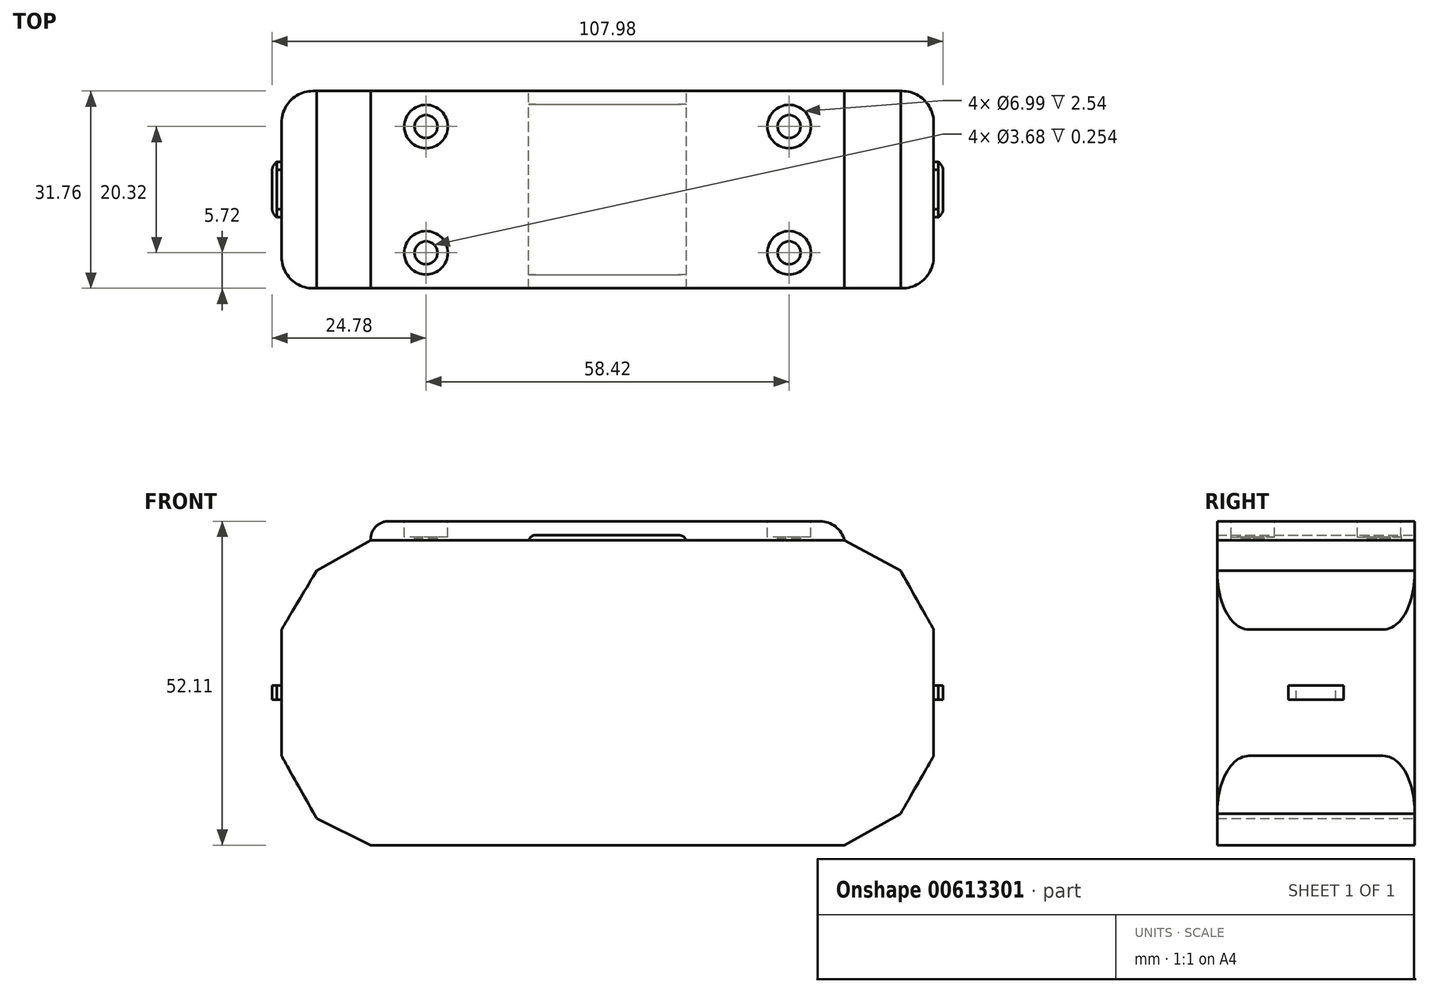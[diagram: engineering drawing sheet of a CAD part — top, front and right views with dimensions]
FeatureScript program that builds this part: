
annotation { "Feature Type Name" : "Feature", "Feature Type Description" : "" }
export const myFeature = defineFeature(function(context is Context, id is Id, definition is map)
    precondition{}
    {
        {
            var Q0;
            Q0=qCreatedBy(makeId("Front.planeOp"),FACE);
            var sketch = newSketch(context, id + "F0", { "sketchPlane" : qUnion([Q0])});
            skLineSegment(sketch, "E0", {"start": v(-38.1, 0) * mm, "end": v(0, 0) * mm});
            skLineSegment(sketch, "E1", {"start": v(0, 0) * mm, "end": v(38.1, 0) * mm});
            skLineSegment(sketch, "E2", {"start": v(-38.1, 0) * mm, "end": v(-52.47, 14.37) * mm});
            skLineSegment(sketch, "E3", {"start": v(38.1, 0) * mm, "end": v(52.47, 14.37) * mm});
            skLineSegment(sketch, "E4", {"start": v(-52.47, 14.37) * mm, "end": v(-52.47, 34.69) * mm});
            skLineSegment(sketch, "E5", {"start": v(52.47, 14.37) * mm, "end": v(52.47, 34.69) * mm});
            skLineSegment(sketch, "E6", {"start": v(-52.47, 34.69) * mm, "end": v(-38.1, 49.06) * mm});
            skLineSegment(sketch, "E7", {"start": v(52.47, 34.69) * mm, "end": v(38.1, 49.06) * mm});
            skLineSegment(sketch, "E8", {"start": v(38.1, 49.06) * mm, "end": v(12.7, 49.06) * mm});
            skLineSegment(sketch, "E9", {"start": v(-38.1, 49.06) * mm, "end": v(-12.7, 49.06) * mm});
            skLineSegment(sketch, "E10", {"start": v(-11.57, 49.9) * mm, "end": v(11.36, 49.9) * mm});
            skArc(sketch, "E11", {"start": v(-11.57, 49.9) * mm, "mid": v(-12.28, 49.66) * mm, "end": v(-12.7, 49.06) * mm});
            skArc(sketch, "E12", {"start": v(12.7, 49.06) * mm, "mid": v(12.15, 49.67) * mm, "end": v(11.36, 49.9) * mm});
            skLineSegment(sketch, "E13", {"start": v(-35.27, 52.11) * mm, "end": v(34.2, 52.11) * mm});
            skArc(sketch, "E14", {"start": v(-35.27, 52.11) * mm, "mid": v(-37.35, 51.2) * mm, "end": v(-38.1, 49.06) * mm});
            skArc(sketch, "E15", {"start": v(38.1, 49.06) * mm, "mid": v(36.67, 51.26) * mm, "end": v(34.2, 52.11) * mm});
            skLineSegment(sketch, "E16", {"start": v(-12.7, 49.06) * mm, "end": v(12.7, 49.06) * mm});
            skLineSegment(sketch, "E17", {"start": v(-52.47, 34.69) * mm, "end": v(-46.81, 44.17) * mm});
            skLineSegment(sketch, "E18", {"start": v(-46.81, 44.17) * mm, "end": v(-38.1, 49.06) * mm});
            skLineSegment(sketch, "E19", {"start": v(52.47, 34.69) * mm, "end": v(47.15, 44.17) * mm});
            skLineSegment(sketch, "E20", {"start": v(47.15, 44.17) * mm, "end": v(38.1, 49.06) * mm});
            skLineSegment(sketch, "E21", {"start": v(-52.47, 14.37) * mm, "end": v(-46.81, 4.29) * mm});
            skLineSegment(sketch, "E22", {"start": v(-46.81, 4.29) * mm, "end": v(-38.1, 0) * mm});
            skLineSegment(sketch, "E23", {"start": v(38.1, 0) * mm, "end": v(47.15, 5.08) * mm});
            skLineSegment(sketch, "E24", {"start": v(47.15, 5.08) * mm, "end": v(52.47, 14.37) * mm});
            skSolve(sketch);
        }
        {
            var Q0;
            Q0=makeQuery(id+"F0.imprint","IMPRINT",FACE,{"disambiguationData":[TD([[makeQuery(id+"F0.imprint","IMPRINT",EDGE,{"derivedFrom":sQuery(id+"F0.wireOp",EDGE,"E0")}),1.0]])]});
            var Q1;
            Q1=makeQuery(id+"F0.imprint","IMPRINT",FACE,{"disambiguationData":[TD([[makeQuery(id+"F0.imprint","IMPRINT",EDGE,{"derivedFrom":sQuery(id+"F0.wireOp",EDGE,"E2")}),1.0]])]});
            var Q2;
            Q2=makeQuery(id+"F0.imprint","IMPRINT",FACE,{"disambiguationData":[TD([[makeQuery(id+"F0.imprint","IMPRINT",EDGE,{"derivedFrom":sQuery(id+"F0.wireOp",EDGE,"E6")}),1.0]])]});
            var Q3;
            Q3=makeQuery(id+"F0.imprint","IMPRINT",FACE,{"disambiguationData":[TD([[makeQuery(id+"F0.imprint","IMPRINT",EDGE,{"derivedFrom":sQuery(id+"F0.wireOp",EDGE,"E7")}),-1.0]])]});
            var Q4;
            Q4=makeQuery(id+"F0.imprint","IMPRINT",FACE,{"disambiguationData":[TD([[makeQuery(id+"F0.imprint","IMPRINT",EDGE,{"derivedFrom":sQuery(id+"F0.wireOp",EDGE,"E3")}),-1.0]])]});
            extrude(context, id + "F1", {"entities" : qUnion([Q0, Q1, Q2, Q3, Q4]), "endBound" : BoundingType.SYMMETRIC, "depth" : 31.75 * mm, "offsetDistance" : 25.4 * mm});
        }
        {
            var Q0;
            Q0=makeQuery(id+"F0.imprint","IMPRINT",FACE,{"disambiguationData":[TD([[makeQuery(id+"F0.imprint","IMPRINT",EDGE,{"derivedFrom":sQuery(id+"F0.wireOp",EDGE,"E8")}),-1.0]])]});
            extrude(context, id + "F2", {"entities" : qUnion([Q0]), "endBound" : BoundingType.SYMMETRIC, "depth" : 31.75 * mm, "offsetDistance" : 25.4 * mm});
        }
        {
            var Q0;
            Q0=makeQuery(id+"F0.imprint","IMPRINT",FACE,{"disambiguationData":[TD([[makeQuery(id+"F0.imprint","IMPRINT",EDGE,{"derivedFrom":sQuery(id+"F0.wireOp",EDGE,"E10")}),-1.0]])]});
            extrude(context, id + "F3", {"entities" : qUnion([Q0]), "endBound" : BoundingType.SYMMETRIC, "depth" : 27.43 * mm, "offsetDistance" : 25.4 * mm});
        }
        {
            var Q0;
            Q0=makeQuery(id+"F2.opExtrude","SWEPT_FACE",FACE,{"disambiguationData":[OSD([sQuery(id+"F0.wireOp",EDGE,"E13")])]});
            var sketch = newSketch(context, id + "F4", { "sketchPlane" : qUnion([Q0])});
            skCircle(sketch, "E25", {"center": v(-29.2, 10.16) * mm, "radius": 3.5 * mm});
            skCircle(sketch, "E26", {"center": v(29.21, 10.16) * mm, "radius": 3.5 * mm});
            skCircle(sketch, "E27", {"center": v(-29.21, -10.16) * mm, "radius": 3.5 * mm});
            skCircle(sketch, "E28", {"center": v(29.21, -10.16) * mm, "radius": 3.5 * mm});
            skCircle(sketch, "E29", {"center": v(29.21, 10.16) * mm, "radius": 1.84 * mm});
            skCircle(sketch, "E30", {"center": v(-29.2, 10.16) * mm, "radius": 1.84 * mm});
            skCircle(sketch, "E31", {"center": v(-29.21, -10.16) * mm, "radius": 1.84 * mm});
            skCircle(sketch, "E32", {"center": v(29.21, -10.16) * mm, "radius": 1.84 * mm});
            skSolve(sketch);
        }
        {
            var Q0;
            {var subQ0=sQuery(id+"F4.wireOp",EDGE,"i9I5KANn-Hw2T-OKhb-yl4n-6DxJZw7aqsBT");var subQ1=sQuery(id+"F4.wireOp",EDGE,"TPdn8FKf-1Wfh-jzqV-Iljf-ABfrrcG5fK8c");var subQ2=makeQuery(id+"F4.imprint","INTERSECT",VERTEX,{"derivedFrom":[subQ1,subQ0]});Q0=makeQuery(id+"F4.imprint","IMPRINT",FACE,{"disambiguationData":[TD([[makeQuery(id+"F4.imprint","IMPRINT",EDGE,{"disambiguationData":[TD([[subQ2,1.0]])],"derivedFrom":subQ1}),-1.0]])]});}
            var Q1;
            {var subQ0=sQuery(id+"F4.wireOp",EDGE,"i9I5KANn-Hw2T-OKhb-yl4n-6DxJZw7aqsBT");var subQ1=sQuery(id+"F4.wireOp",EDGE,"TPdn8FKf-1Wfh-jzqV-Iljf-ABfrrcG5fK8c");var subQ2=makeQuery(id+"F4.imprint","INTERSECT",VERTEX,{"derivedFrom":[subQ1,subQ0]});Q1=makeQuery(id+"F4.imprint","IMPRINT",FACE,{"disambiguationData":[TD([[makeQuery(id+"F4.imprint","IMPRINT",EDGE,{"disambiguationData":[TD([[subQ2,1.0]])],"derivedFrom":subQ1}),1.0]])]});}
            var Q2;
            {var subQ0=sQuery(id+"F4.wireOp",EDGE,"VOcv5QYX-RCKe-hodg-bxS0-XieY8gz3RQ9G");var subQ1=sQuery(id+"F4.wireOp",EDGE,"O975SV0D-9PoP-xruf-v8xU-hlFepfZSX1na");var subQ2=makeQuery(id+"F4.imprint","INTERSECT",VERTEX,{"derivedFrom":[subQ1,subQ0]});Q2=makeQuery(id+"F4.imprint","IMPRINT",FACE,{"disambiguationData":[TD([[makeQuery(id+"F4.imprint","IMPRINT",EDGE,{"disambiguationData":[TD([[subQ2,1.0]])],"derivedFrom":subQ1}),-1.0]])]});}
            var Q3;
            {var subQ0=sQuery(id+"F4.wireOp",EDGE,"VOcv5QYX-RCKe-hodg-bxS0-XieY8gz3RQ9G");var subQ1=sQuery(id+"F4.wireOp",EDGE,"O975SV0D-9PoP-xruf-v8xU-hlFepfZSX1na");var subQ2=makeQuery(id+"F4.imprint","INTERSECT",VERTEX,{"derivedFrom":[subQ1,subQ0]});Q3=makeQuery(id+"F4.imprint","IMPRINT",FACE,{"disambiguationData":[TD([[makeQuery(id+"F4.imprint","IMPRINT",EDGE,{"disambiguationData":[TD([[subQ2,1.0]])],"derivedFrom":subQ1}),1.0]])]});}
            var Q4;
            Q4=makeQuery(id+"F4.imprint","IMPRINT",FACE,{"disambiguationData":[TD([[makeQuery(id+"F4.imprint","IMPRINT",EDGE,{"derivedFrom":sQuery(id+"F4.wireOp",EDGE,"E28")}),1.0]])]});
            var Q5;
            Q5=makeQuery(id+"F4.imprint","IMPRINT",FACE,{"disambiguationData":[TD([[makeQuery(id+"F4.imprint","IMPRINT",EDGE,{"derivedFrom":sQuery(id+"F4.wireOp",EDGE,"E27")}),1.0]])]});
            var Q6;
            Q6=makeQuery(id+"F4.imprint","IMPRINT",FACE,{"disambiguationData":[TD([[makeQuery(id+"F4.imprint","IMPRINT",EDGE,{"derivedFrom":sQuery(id+"F4.wireOp",EDGE,"E25")}),1.0]])]});
            var Q7;
            Q7=makeQuery(id+"F4.imprint","IMPRINT",FACE,{"disambiguationData":[TD([[makeQuery(id+"F4.imprint","IMPRINT",EDGE,{"derivedFrom":sQuery(id+"F4.wireOp",EDGE,"E26")}),1.0]])]});
            extrude(context, id + "F5", {"entities" : qUnion([Q0, Q1, Q2, Q3, Q4, Q5, Q6, Q7]), "operationType" : NewBodyOperationType.REMOVE, "oppositeDirection" : true, "depth" : 2.54 * mm, "offsetDistance" : 25.4 * mm});
        }
        {
            var Q0;
            Q0=makeQuery(id+"F4.imprint","IMPRINT",FACE,{"disambiguationData":[TD([[makeQuery(id+"F4.imprint","IMPRINT",EDGE,{"derivedFrom":sQuery(id+"F4.wireOp",EDGE,"E31")}),1.0]])]});
            var Q1;
            Q1=makeQuery(id+"F4.imprint","IMPRINT",FACE,{"disambiguationData":[TD([[makeQuery(id+"F4.imprint","IMPRINT",EDGE,{"derivedFrom":sQuery(id+"F4.wireOp",EDGE,"E29")}),1.0]])]});
            var Q2;
            Q2=makeQuery(id+"F4.imprint","IMPRINT",FACE,{"disambiguationData":[TD([[makeQuery(id+"F4.imprint","IMPRINT",EDGE,{"derivedFrom":sQuery(id+"F4.wireOp",EDGE,"E32")}),1.0]])]});
            var Q3;
            Q3=makeQuery(id+"F4.imprint","IMPRINT",FACE,{"disambiguationData":[TD([[makeQuery(id+"F4.imprint","IMPRINT",EDGE,{"derivedFrom":sQuery(id+"F4.wireOp",EDGE,"E30")}),1.0]])]});
            extrude(context, id + "F6", {"entities" : qUnion([Q0, Q1, Q2, Q3]), "operationType" : NewBodyOperationType.REMOVE, "oppositeDirection" : true, "depth" : 2.8 * mm, "offsetDistance" : 25.4 * mm});
        }
        {
            var Q0;
            Q0=makeQuery(id+"F1.opExtrude","SWEPT_FACE",FACE,{"disambiguationData":[OSD([sQuery(id+"F0.wireOp",EDGE,"E4")])]});
            var sketch = newSketch(context, id + "F7", { "sketchPlane" : qUnion([Q0])});
            skLineSegment(sketch, "E33", {"start": v(0, 34.69) * mm, "end": v(0, 14.37) * mm});
            skLineSegment(sketch, "E34", {"start": v(-15.88, 24.53) * mm, "end": v(15.88, 24.53) * mm});
            skLineSegment(sketch, "E35", {"start": v(-4.45, 24.53) * mm, "end": v(-4.45, 25.67) * mm});
            skLineSegment(sketch, "E36", {"start": v(4.45, 24.53) * mm, "end": v(4.45, 25.67) * mm});
            skLineSegment(sketch, "E37", {"start": v(4.45, 25.67) * mm, "end": v(3.18, 25.67) * mm});
            skLineSegment(sketch, "E38", {"start": v(3.18, 25.67) * mm, "end": v(3.18, 24.53) * mm});
            skLineSegment(sketch, "E39", {"start": v(-4.45, 25.67) * mm, "end": v(-3.18, 25.67) * mm});
            skLineSegment(sketch, "E40", {"start": v(-3.17, 25.67) * mm, "end": v(-3.17, 24.53) * mm});
            skLineSegment(sketch, "E41", {"start": v(-4.45, 24.53) * mm, "end": v(-4.45, 23.39) * mm});
            skLineSegment(sketch, "E42", {"start": v(4.45, 24.53) * mm, "end": v(4.45, 23.39) * mm});
            skLineSegment(sketch, "E43", {"start": v(-3.17, 24.53) * mm, "end": v(-3.17, 23.39) * mm});
            skLineSegment(sketch, "E44", {"start": v(-3.17, 23.39) * mm, "end": v(-4.45, 23.39) * mm});
            skLineSegment(sketch, "E45", {"start": v(3.18, 24.53) * mm, "end": v(3.18, 23.39) * mm});
            skLineSegment(sketch, "E46", {"start": v(3.18, 23.39) * mm, "end": v(4.45, 23.39) * mm});
            skLineSegment(sketch, "E47", {"start": v(3.18, 24.53) * mm, "end": v(-3.17, 24.53) * mm});
            skSolve(sketch);
        }
        {
            var Q0;
            {var subQ0=sQuery(id+"F7.wireOp",EDGE,"E35");Q0=makeQuery(id+"F7.imprint","IMPRINT",FACE,{"disambiguationData":[TD([[makeQuery(id+"F7.imprint","IMPRINT",EDGE,{"derivedFrom":subQ0}),-1.0]])]});}
            var Q1;
            {var subQ0=sQuery(id+"F7.wireOp",EDGE,"E41");Q1=makeQuery(id+"F7.imprint","IMPRINT",FACE,{"disambiguationData":[TD([[makeQuery(id+"F7.imprint","IMPRINT",EDGE,{"derivedFrom":subQ0}),1.0]])]});}
            var Q2;
            {var subQ0=sQuery(id+"F7.wireOp",EDGE,"E36");Q2=makeQuery(id+"F7.imprint","IMPRINT",FACE,{"disambiguationData":[TD([[makeQuery(id+"F7.imprint","IMPRINT",EDGE,{"derivedFrom":subQ0}),1.0]])]});}
            var Q3;
            {var subQ0=sQuery(id+"F7.wireOp",EDGE,"E42");Q3=makeQuery(id+"F7.imprint","IMPRINT",FACE,{"disambiguationData":[TD([[makeQuery(id+"F7.imprint","IMPRINT",EDGE,{"derivedFrom":subQ0}),-1.0]])]});}
            extrude(context, id + "F8", {"entities" : qUnion([Q0, Q1, Q2, Q3]), "depth" : 0.76 * mm, "offsetDistance" : 25.4 * mm});
        }
        {
            var Q0;
            Q0=makeQuery(id+"F8.opExtrude","CAP_FACE",FACE,{"disambiguationData":[OSD([sQuery(id+"F7.wireOp",EDGE,"E35"),sQuery(id+"F7.wireOp",EDGE,"E39"),sQuery(id+"F7.wireOp",EDGE,"E40"),sQuery(id+"F7.wireOp",EDGE,"E41"),sQuery(id+"F7.wireOp",EDGE,"E43"),sQuery(id+"F7.wireOp",EDGE,"E44")])],"isStart":false});
            var sketch = newSketch(context, id + "F9", { "sketchPlane" : qUnion([Q0])});
            skLineSegment(sketch, "E48.0.3", {"start": v(4.45, 23.39) * mm, "end": v(4.45, 25.67) * mm});
            skLineSegment(sketch, "E49", {"start": v(-4.45, 25.67) * mm, "end": v(-4.45, 23.39) * mm});
            skLineSegment(sketch, "E50", {"start": v(-4.45, 23.39) * mm, "end": v(4.45, 23.39) * mm});
            skLineSegment(sketch, "E51", {"start": v(4.45, 25.67) * mm, "end": v(-4.45, 25.67) * mm});
            skSolve(sketch);
        }
        {
            var Q0;
            Q0 = qSketchRegion(id + "F9", true);
            extrude(context, id + "F10", {"entities" : qUnion([Q0]), "depth" : 0.76 * mm, "offsetDistance" : 25.4 * mm});
        }
        {
            var Q0;
            Q0=makeQuery(id+"F1.opExtrude","CAP_EDGE",EDGE,{"disambiguationData":[OSD([sQuery(id+"F0.wireOp",EDGE,"E4")])],"isStart":false});
            var Q1;
            Q1=makeQuery(id+"F1.opExtrude","CAP_EDGE",EDGE,{"disambiguationData":[OSD([sQuery(id+"F0.wireOp",EDGE,"E4")])],"isStart":true});
            var Q2;
            Q2=makeQuery(id+"F1.opExtrude","CAP_EDGE",EDGE,{"disambiguationData":[OSD([sQuery(id+"F0.wireOp",EDGE,"E5")])],"isStart":false});
            var Q3;
            Q3=makeQuery(id+"F1.opExtrude","CAP_EDGE",EDGE,{"disambiguationData":[OSD([sQuery(id+"F0.wireOp",EDGE,"E5")])],"isStart":true});
            fillet(context, id + "F11", {"entities" : qUnion([Q0, Q1, Q2, Q3]), "radius" : 5.08 * mm, "tangentPropagation" : true, "allowEdgeOverflow" : false});
        }
        {
            var Q0;
            Q0=makeQuery(id+"F1.opExtrude","SWEPT_FACE",FACE,{"disambiguationData":[OSD([sQuery(id+"F0.wireOp",EDGE,"E5")])]});
            var sketch = newSketch(context, id + "F12", { "sketchPlane" : qUnion([Q0])});
            skSolve(sketch);
        }
        {
            var Q0;
            {var subQ0=sQuery(id+"F0.wireOp",EDGE,"E5");Q0=makeQuery(id+"F12.imprint","IMPRINT",FACE,{"disambiguationData":[TD([[makeQuery(id+"F12.imprint","IMPRINT",EDGE,{"derivedFrom":makeQuery(id+"F1.opExtrude","SWEPT_EDGE",EDGE,{"disambiguationData":[OSD([sQuery(id+"F0.wireOp",EDGE,"E3"),subQ0])]})}),1.0]])]});}
            var sketch = newSketch(context, id + "F13", { "sketchPlane" : qUnion([Q0])});
            skLineSegment(sketch, "E52.0", {"start": v(-10.8, 34.69) * mm, "end": v(-10.8, 14.37) * mm});
            skLineSegment(sketch, "E52.1", {"start": v(-10.8, 34.69) * mm, "end": v(10.8, 34.69) * mm});
            skLineSegment(sketch, "E52.2", {"start": v(10.8, 14.37) * mm, "end": v(10.8, 34.69) * mm});
            skLineSegment(sketch, "E52.3", {"start": v(-10.8, 14.37) * mm, "end": v(10.8, 14.37) * mm});
            skLineSegment(sketch, "E53", {"start": v(0, 34.69) * mm, "end": v(0, 14.37) * mm});
            skLineSegment(sketch, "E54", {"start": v(0, 24.53) * mm, "end": v(3.18, 24.53) * mm});
            skLineSegment(sketch, "E55", {"start": v(0, 24.53) * mm, "end": v(-3.18, 24.53) * mm});
            skLineSegment(sketch, "E56", {"start": v(-3.18, 24.53) * mm, "end": v(-3.18, 25.67) * mm});
            skLineSegment(sketch, "E57", {"start": v(-3.18, 25.67) * mm, "end": v(-4.45, 25.67) * mm});
            skLineSegment(sketch, "E58", {"start": v(-4.45, 25.67) * mm, "end": v(-4.45, 23.39) * mm});
            skLineSegment(sketch, "E59", {"start": v(-4.45, 23.39) * mm, "end": v(-3.18, 23.39) * mm});
            skLineSegment(sketch, "E60", {"start": v(-3.18, 23.39) * mm, "end": v(-3.18, 24.53) * mm});
            skLineSegment(sketch, "E61", {"start": v(3.18, 24.53) * mm, "end": v(3.18, 23.39) * mm});
            skLineSegment(sketch, "E62", {"start": v(3.18, 23.39) * mm, "end": v(3.18, 25.67) * mm});
            skLineSegment(sketch, "E63", {"start": v(3.18, 25.67) * mm, "end": v(4.45, 25.67) * mm});
            skLineSegment(sketch, "E64", {"start": v(4.45, 25.67) * mm, "end": v(4.45, 23.39) * mm});
            skLineSegment(sketch, "E65", {"start": v(4.45, 23.39) * mm, "end": v(3.18, 23.39) * mm});
            skSolve(sketch);
        }
        {
            var Q0;
            Q0=makeQuery(id+"F13.imprint","IMPRINT",FACE,{"disambiguationData":[TD([[makeQuery(id+"F13.imprint","IMPRINT",EDGE,{"derivedFrom":sQuery(id+"F13.wireOp",EDGE,"E56")}),1.0]])]});
            var Q1;
            {var subQ0=sQuery(id+"F13.wireOp",EDGE,"E63");Q1=makeQuery(id+"F13.imprint","IMPRINT",FACE,{"disambiguationData":[TD([[makeQuery(id+"F13.imprint","IMPRINT",EDGE,{"derivedFrom":subQ0}),-1.0]])]});}
            extrude(context, id + "F14", {"entities" : qUnion([Q0, Q1]), "depth" : 0.76 * mm, "offsetDistance" : 25.4 * mm});
        }
        {
            var Q0;
            Q0=makeQuery(id+"F14.opExtrude","CAP_FACE",FACE,{"disambiguationData":[OSD([sQuery(id+"F13.wireOp",EDGE,"E56"),sQuery(id+"F13.wireOp",EDGE,"E57"),sQuery(id+"F13.wireOp",EDGE,"E58"),sQuery(id+"F13.wireOp",EDGE,"E59"),sQuery(id+"F13.wireOp",EDGE,"E60")])],"isStart":false});
            var sketch = newSketch(context, id + "F15", { "sketchPlane" : qUnion([Q0])});
            skLineSegment(sketch, "E66.0.2", {"start": v(4.45, 23.39) * mm, "end": v(4.45, 25.67) * mm});
            skLineSegment(sketch, "E67", {"start": v(-4.45, 23.39) * mm, "end": v(-4.45, 25.67) * mm});
            skLineSegment(sketch, "E68", {"start": v(-4.45, 25.67) * mm, "end": v(4.45, 25.67) * mm});
            skLineSegment(sketch, "E69", {"start": v(-4.45, 23.39) * mm, "end": v(4.45, 23.39) * mm});
            skSolve(sketch);
        }
        {
            var Q0;
            Q0 = qSketchRegion(id + "F15", true);
            extrude(context, id + "F16", {"entities" : qUnion([Q0]), "depth" : 0.76 * mm, "offsetDistance" : 25.4 * mm});
        }
        {
            var Q0;
            Q0=makeQuery(id+"F10.opExtrude","CAP_EDGE",EDGE,{"disambiguationData":[OSD([sQuery(id+"F9.wireOp",EDGE,"E49")])],"isStart":false});
            var Q1;
            Q1=makeQuery(id+"F10.opExtrude","CAP_EDGE",EDGE,{"disambiguationData":[OSD([sQuery(id+"F9.wireOp",EDGE,"E48.0.3")])],"isStart":false});
            var Q2;
            Q2=makeQuery(id+"F16.opExtrude","CAP_EDGE",EDGE,{"disambiguationData":[OSD([sQuery(id+"F15.wireOp",EDGE,"E67")])],"isStart":false});
            var Q3;
            Q3=makeQuery(id+"F16.opExtrude","CAP_EDGE",EDGE,{"disambiguationData":[OSD([sQuery(id+"F15.wireOp",EDGE,"E66.0.2")])],"isStart":false});
            fillet(context, id + "F17", {"entities" : qUnion([Q0, Q1, Q2, Q3]), "radius" : 1.78 * mm, "tangentPropagation" : true, "allowEdgeOverflow" : false});
        }
    });
